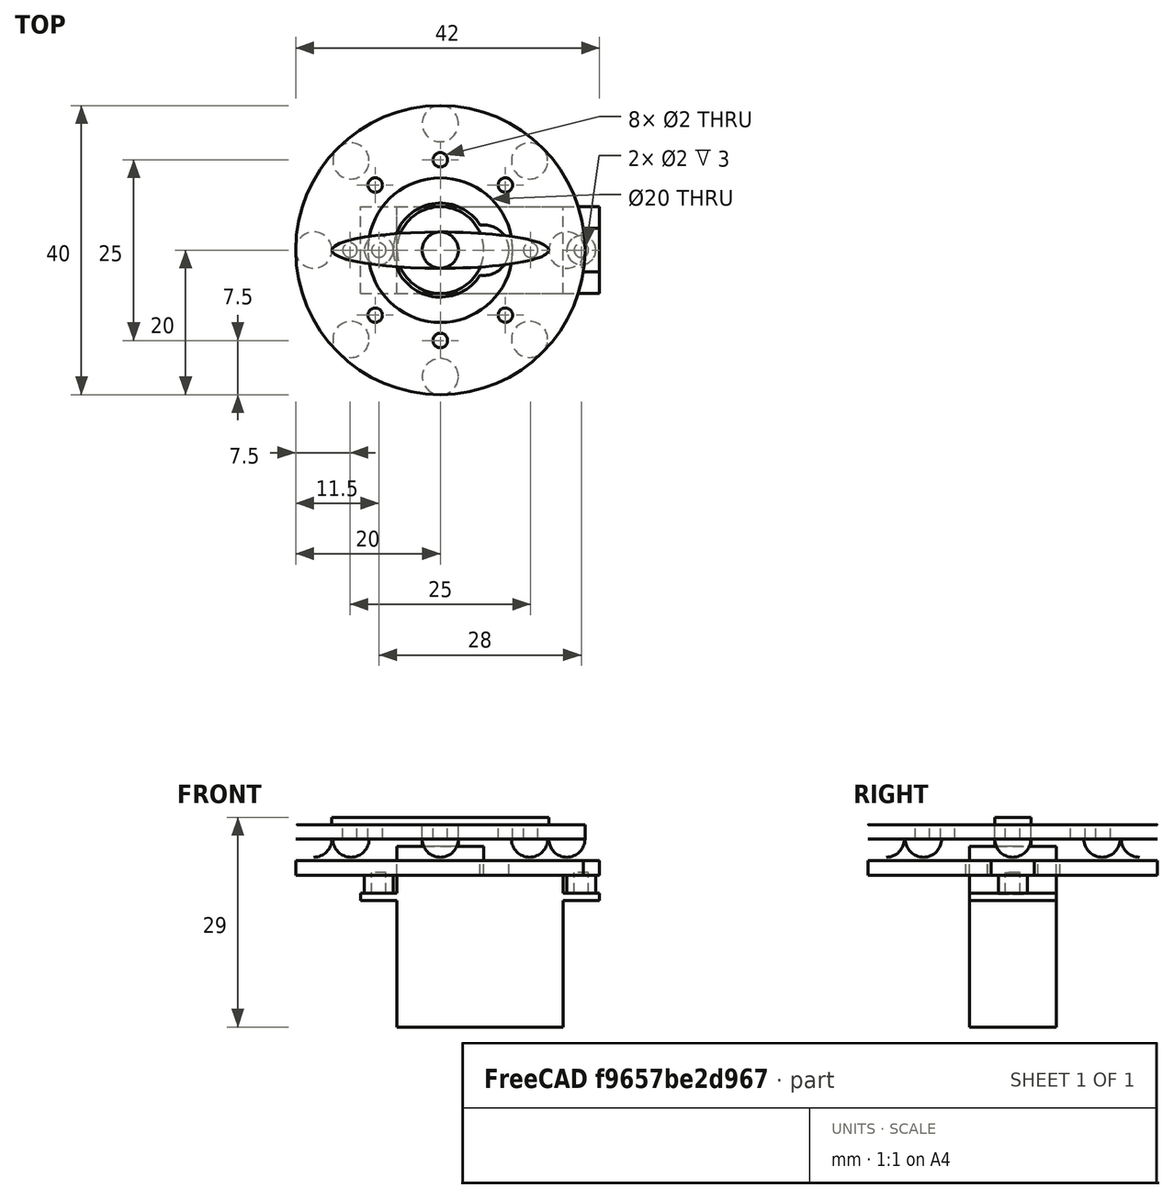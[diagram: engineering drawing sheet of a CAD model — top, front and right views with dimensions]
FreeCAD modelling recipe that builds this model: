
FCSTD DOCUMENT
Label: ServoL
License: CC-BY 3.0
LicenseURL: http://creativecommons.org/licenses/by/3.0/
objects: Part::Cylinder×20, Part::Sphere×8, Part::MultiFuse×7, Part::Box×3, Part::Cut×2, Part::FeaturePython×1
note: 41 computed .brp shape members not serialized (recipe doc carries the construction recipe); baked Part::Feature solids carry a one-line shape summary decoded from their .brp

FEATURE [Part::Box] Box  label="ServoBody"
  Height = 21
  Length = 23
  Width = 12
FEATURE [Part::Cylinder] Cylinder  label="ServoBody2"
  Angle = 360
  Height = 4
  Placement = pos=(6,6,21) rot=(0,0,1;0rad)
  Radius = 6
FEATURE [Part::Box] Box001  label="ServoBody3"
  Height = 1
  Length = 33
  Placement = pos=(-5,0,17.5) rot=(0,0,1;0rad)
  Width = 12
FEATURE [Part::Cylinder] Cylinder001  label="ServoAxis"
  Angle = 360
  Height = 4
  Placement = pos=(6,6,24) rot=(0,0,1;0rad)
  Radius = 2.5
FEATURE [Part::MultiFuse] Fusion005  label="ServoArmL"
  Shapes = -> [Cylinder001,Box001,Box,Cylinder]
FEATURE [Part::Cylinder] Cylinder002
  Angle = 360
  Height = 2
  Radius = 2.5
FEATURE [Part::FeaturePython] Scale  # Draft clone (typed FeaturePython)
  Objects = -> [Cylinder002]
  Placement = pos=(0,0,1) rot=(0,0,1;0rad)
  Scale = (6,1,0.5)
FEATURE [Part::MultiFuse] Fusion  label="Arm"
  Placement = pos=(6,6,27) rot=(0,0,1;0rad)
  Shapes = -> [Cylinder002,Scale]
FEATURE [Part::MultiFuse] Fusion006  label="Servo"
  Shapes = -> [Fusion005,Fusion]
FEATURE [Part::Cylinder] Cylinder003001001003  label="Cylinder008"
  Angle = 360
  Height = 2
  Placement = pos=(6,6,26) rot=(0,0,1;0rad)
  Radius = 20
FEATURE [Part::Cylinder] Cylinder003001001004  label="Cylinder009"
  Angle = 360
  Height = 3
  Placement = pos=(-2.5,6,18.4) rot=(0,0,1;0rad)
  Radius = 2
FEATURE [Part::Cylinder] Cylinder003001001005  label="Cylinder011"
  Angle = 360
  Height = 2
  Placement = pos=(6,6,21) rot=(0,0,1;0rad)
  Radius = 20
FEATURE [Part::Cylinder] Cylinder003001001004001  label="Cylinder010"
  Angle = 360
  Height = 3
  Placement = pos=(25.5,6,18.4) rot=(0,0,1;0rad)
  Radius = 2
FEATURE [Part::Cylinder] Cylinder003001001005001  label="Cylinder012"
  Angle = 360
  Height = 2
  Placement = pos=(6,6,21) rot=(0,0,1;0rad)
  Radius = 6.5
FEATURE [Part::Cylinder] Cylinder003001001005001001  label="Cylinder013"
  Angle = 360
  Height = 2
  Placement = pos=(12,6,21) rot=(0,0,1;0rad)
  Radius = 3.5
FEATURE [Part::Box] Box002
  Height = 2
  Length = 10
  Placement = pos=(18,3,21) rot=(0,0,1;0rad)
  Width = 6
FEATURE [Part::Cylinder] Cylinder003001001004002  label="Cylinder014"
  Angle = 360
  Height = 5
  Placement = pos=(-2.5,6,16.4) rot=(0,0,1;0rad)
  Radius = 1
FEATURE [Part::Cylinder] Cylinder003001001004001001  label="Cylinder015"
  Angle = 360
  Height = 5
  Placement = pos=(25.5,6,16.4) rot=(0,0,1;0rad)
  Radius = 1
FEATURE [Part::MultiFuse] Fusion008
  Shapes = -> [Cylinder003001001005,Box002,Cylinder003001001004,Cylinder003001001004001]
FEATURE [Part::MultiFuse] Fusion009
  Shapes = -> [Cylinder003001001005001,Cylinder003001001005001001,Cylinder003001001004002,Cylinder003001001004001001]
FEATURE [Part::Cut] Cut002  label="Guide1"
  Base = -> Fusion008
  Tool = -> Fusion009
FEATURE [Part::Sphere] Sphere
  Angle1 = -90
  Angle2 = 0
  Angle3 = 360
  Placement = pos=(-6.35,-6.35,26) rot=(0,0,1;0rad)
  Radius = 2.5
FEATURE [Part::Sphere] Sphere001
  Angle1 = -90
  Angle2 = 0
  Angle3 = 360
  Placement = pos=(18.35,-6.35,26) rot=(0,0,1;0rad)
  Radius = 2.5
FEATURE [Part::Sphere] Sphere001001  label="Sphere002"
  Angle1 = -90
  Angle2 = 0
  Angle3 = 360
  Placement = pos=(18.35,18.35,26) rot=(0,0,1;0rad)
  Radius = 2.5
FEATURE [Part::Sphere] Sphere001001001  label="Sphere003"
  Angle1 = -90
  Angle2 = 0
  Angle3 = 360
  Placement = pos=(-6.35,18.35,26) rot=(0,0,1;0rad)
  Radius = 2.5
FEATURE [Part::Cylinder] Cylinder003001001005001004  label="Cylinder020"
  Angle = 360
  Height = 4
  Placement = pos=(-6.5,6,26) rot=(0,0,1;0rad)
  Radius = 1
FEATURE [Part::Cylinder] Cylinder003001001001003  label="Cylinder021"
  Angle = 360
  Height = 4
  Placement = pos=(18.5,6,26) rot=(0,0,1;0rad)
  Radius = 1
FEATURE [Part::Cylinder] Cylinder003001001005001003001  label="Cylinder022"
  Angle = 360
  Height = 5
  Placement = pos=(-3,-3,26) rot=(0,0,1;0rad)
  Radius = 1
FEATURE [Part::Cylinder] Cylinder003001001001002001  label="Cylinder023"
  Angle = 360
  Height = 5
  Placement = pos=(15,-3,26) rot=(0,0,1;0rad)
  Radius = 1
FEATURE [Part::Sphere] Sphere001001001001  label="Sphere004"
  Angle1 = -90
  Angle2 = 0
  Angle3 = 360
  Placement = pos=(-11.5,6,26) rot=(0,0,1;0rad)
  Radius = 2.5
FEATURE [Part::Sphere] Sphere001001001001001  label="Sphere005"
  Angle1 = -90
  Angle2 = 0
  Angle3 = 360
  Placement = pos=(23.5,6,26) rot=(0,0,1;0rad)
  Radius = 2.5
FEATURE [Part::Sphere] Sphere001001001001001001  label="Sphere006"
  Angle1 = -90
  Angle2 = 0
  Angle3 = 360
  Placement = pos=(6,-11.5,26) rot=(0,0,1;0rad)
  Radius = 2.5
FEATURE [Part::Sphere] Sphere001001001001001001001  label="Sphere007"
  Angle1 = -90
  Angle2 = 0
  Angle3 = 360
  Placement = pos=(6,23.5,26) rot=(0,0,1;0rad)
  Radius = 2.5
FEATURE [Part::Cylinder] Cylinder003001001003001  label="Cylinder024"
  Angle = 360
  Height = 2
  Placement = pos=(6,6,26) rot=(0,0,1;0rad)
  Radius = 10
FEATURE [Part::MultiFuse] Fusion014
  Shapes = -> [Sphere,Cylinder003001001003,Sphere001001001,Sphere001001001001001001,Sphere001001001001,Sphere001,Sphere001001,Sphere001001001001001001001,Sphere001001001001001]
FEATURE [Part::Cylinder] Cylinder003001001005001003001001  label="Cylinder025"
  Angle = 360
  Height = 5
  Placement = pos=(-3,15,26) rot=(0,0,1;0rad)
  Radius = 1
FEATURE [Part::Cylinder] Cylinder003001001001002001001  label="Cylinder026"
  Angle = 360
  Height = 5
  Placement = pos=(15,15,26) rot=(0,0,1;0rad)
  Radius = 1
FEATURE [Part::Cylinder] Cylinder003001001005001003001001001  label="Cylinder027"
  Angle = 360
  Height = 5
  Placement = pos=(6,18.5,26) rot=(0,0,1;0rad)
  Radius = 1
FEATURE [Part::Cylinder] Cylinder003001001005001003001001001001  label="Cylinder028"
  Angle = 360
  Height = 5
  Placement = pos=(6,-6.5,26) rot=(0,0,1;0rad)
  Radius = 1
FEATURE [Part::MultiFuse] Fusion015
  Shapes = -> [Cylinder003001001003001,Cylinder003001001005001004,Cylinder003001001001003,Cylinder003001001005001003001,Cylinder003001001001002001,Cylinder003001001005001003001001,Cylinder003001001005001003001001001001,Cylinder003001001001002001001,Cylinder003001001005001003001001001]
FEATURE [Part::Cut] Cut  label="Guide2"
  Base = -> Fusion014
  Tool = -> Fusion015
